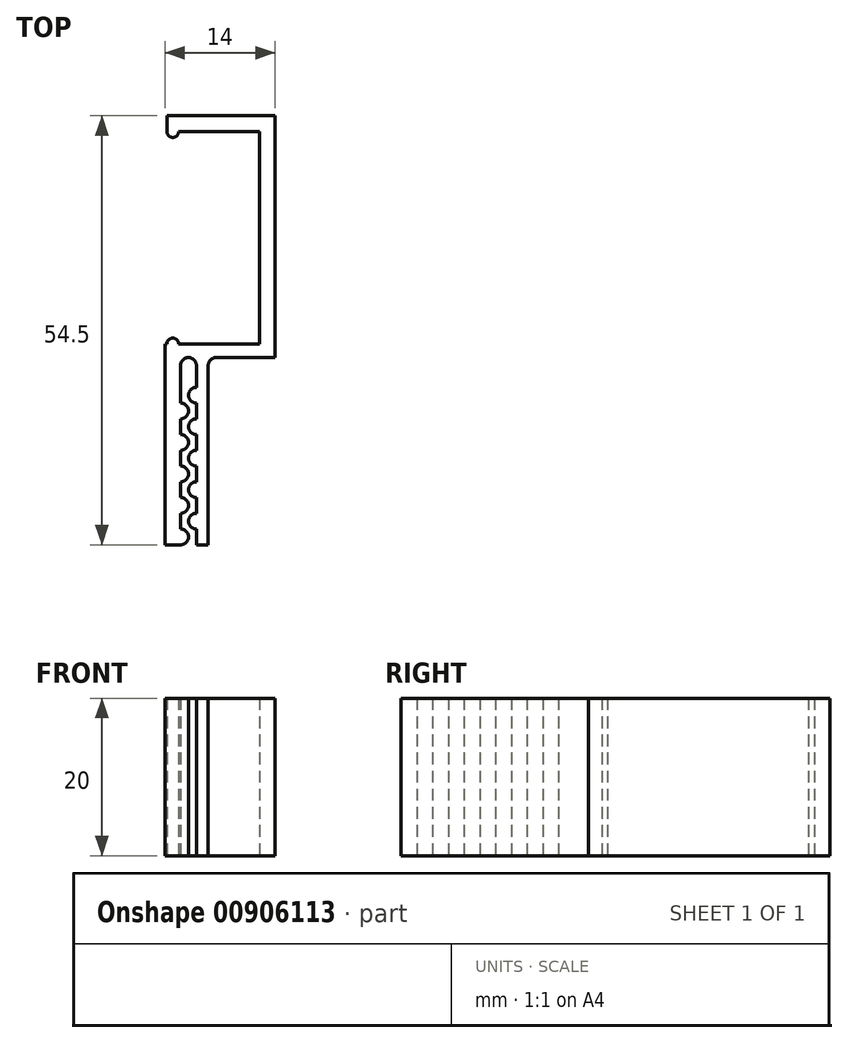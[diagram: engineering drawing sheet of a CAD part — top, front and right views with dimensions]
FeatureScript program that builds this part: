
annotation { "Feature Type Name" : "Feature", "Feature Type Description" : "" }
export const myFeature = defineFeature(function(context is Context, id is Id, definition is map)
    precondition{}
    {
        {
            var Q0;
            Q0=qCreatedBy(makeId("Top.planeOp"),FACE);
            var sketch = newSketch(context, id + "F0", { "sketchPlane" : qUnion([Q0])});
            skLineSegment(sketch, "E0", {"start": v(0, 0) * mm, "end": v(0, 25.5) * mm});
            skLineSegment(sketch, "E1", {"start": v(12, 25.5) * mm, "end": v(12, 52.5) * mm});
            skLineSegment(sketch, "E2", {"start": v(12, 52.5) * mm, "end": v(1.75, 52.5) * mm});
            skLineSegment(sketch, "E3.0", {"start": v(14, 54.5) * mm, "end": v(0.25, 54.5) * mm});
            skLineSegment(sketch, "E3.1", {"start": v(14, 23.78) * mm, "end": v(14, 54.5) * mm});
            skLineSegment(sketch, "E3.2", {"start": v(3, 23.78) * mm, "end": v(3, 23.78) * mm});
            skLineSegment(sketch, "E3.3", {"start": v(2, 2) * mm, "end": v(2, 5) * mm});
            skLineSegment(sketch, "E4", {"start": v(0, 0) * mm, "end": v(2, 0) * mm});
            skLineSegment(sketch, "E5.trimOffspring", {"start": v(1.75, 25.5) * mm, "end": v(12, 25.5) * mm});
            skLineSegment(sketch, "E6.0", {"start": v(4, 0) * mm, "end": v(4, 2) * mm});
            skLineSegment(sketch, "E7.0", {"start": v(5.5, 0) * mm, "end": v(5.5, 22.78) * mm});
            skLineSegment(sketch, "E8", {"start": v(4, 0) * mm, "end": v(5.5, 0) * mm});
            skLineSegment(sketch, "E9.trimOffspring", {"start": v(6.5, 23.78) * mm, "end": v(14, 23.78) * mm});
            skArc(sketch, "E10", {"start": v(2, 0) * mm, "mid": v(3, 1) * mm, "end": v(2, 2) * mm});
            skArc(sketch, "E11", {"start": v(4, 4) * mm, "mid": v(3, 3) * mm, "end": v(4, 2) * mm});
            skArc(sketch, "E12.0.1.0", {"start": v(2, 4) * mm, "mid": v(3, 5) * mm, "end": v(2, 6) * mm});
            skArc(sketch, "E12.0.1.1", {"start": v(4, 8) * mm, "mid": v(3, 7) * mm, "end": v(4, 6) * mm});
            skArc(sketch, "E12.0.2.0", {"start": v(2, 8) * mm, "mid": v(3, 9) * mm, "end": v(2, 10) * mm});
            skArc(sketch, "E12.0.2.1", {"start": v(4, 12) * mm, "mid": v(3, 11) * mm, "end": v(4, 10) * mm});
            skArc(sketch, "E12.0.3.0", {"start": v(2, 12) * mm, "mid": v(3, 13) * mm, "end": v(2, 14) * mm});
            skArc(sketch, "E12.0.3.1", {"start": v(4, 16) * mm, "mid": v(3, 15) * mm, "end": v(4, 14) * mm});
            skArc(sketch, "E12.0.4.0", {"start": v(2, 16) * mm, "mid": v(3, 17) * mm, "end": v(2, 18) * mm});
            skArc(sketch, "E12.0.4.1", {"start": v(4, 20) * mm, "mid": v(3, 19) * mm, "end": v(4, 18) * mm});
            skLineSegment(sketch, "E12.direction1", {"start": v(2, 1) * mm, "end": v(27, 1) * mm, "construction": true});
            skLineSegment(sketch, "E12.direction2", {"start": v(2, 2) * mm, "end": v(2, 4) * mm, "construction": true});
            skLineSegment(sketch, "E13.trimOffspring", {"start": v(4, 20) * mm, "end": v(4, 22.78) * mm});
            skLineSegment(sketch, "E14.trimOffspring", {"start": v(2, 18) * mm, "end": v(2, 22.78) * mm});
            skLineSegment(sketch, "E15.trimOffspring", {"start": v(4, 16) * mm, "end": v(4, 18) * mm});
            skLineSegment(sketch, "E16.trimOffspring", {"start": v(2, 14) * mm, "end": v(2, 16) * mm});
            skLineSegment(sketch, "E17.trimOffspring", {"start": v(4, 12) * mm, "end": v(4, 14) * mm});
            skLineSegment(sketch, "E18.trimOffspring", {"start": v(2, 10) * mm, "end": v(2, 12) * mm});
            skLineSegment(sketch, "E19.trimOffspring", {"start": v(4, 8) * mm, "end": v(4, 10) * mm});
            skLineSegment(sketch, "E20.trimOffspring", {"start": v(2, 6) * mm, "end": v(2, 8) * mm});
            skLineSegment(sketch, "E21.trimOffspring", {"start": v(4, 4) * mm, "end": v(4, 6) * mm});
            skPoint(sketch, "E22.visualSharp", {"position": v(4, 23.78) * mm});
            skArc(sketch, "E22.filletArc", {"start": v(4, 22.78) * mm, "mid": v(3.7, 23.48) * mm, "end": v(3, 23.78) * mm});
            skPoint(sketch, "E23.visualSharp", {"position": v(2, 23.78) * mm});
            skArc(sketch, "E23.filletArc", {"start": v(3, 23.78) * mm, "mid": v(2.3, 23.48) * mm, "end": v(2, 22.78) * mm});
            skPoint(sketch, "E24.visualSharp", {"position": v(5.5, 23.78) * mm});
            skArc(sketch, "E24.filletArc", {"start": v(6.5, 23.78) * mm, "mid": v(5.8, 23.48) * mm, "end": v(5.5, 22.78) * mm});
            skLineSegment(sketch, "E25", {"start": v(0.25, 54.5) * mm, "end": v(0.25, 52.5) * mm});
            skArc(sketch, "E26", {"start": v(1.75, 25.5) * mm, "mid": v(1, 26.25) * mm, "end": v(0.25, 25.5) * mm});
            skArc(sketch, "E27", {"start": v(0.25, 52.5) * mm, "mid": v(1, 51.75) * mm, "end": v(1.75, 52.5) * mm});
            skLineSegment(sketch, "E28", {"start": v(0.25, 25.5) * mm, "end": v(0, 25.5) * mm});
            skSolve(sketch);
        }
        {
            var Q0;
            Q0=makeQuery(id+"F0.imprint","IMPRINT",FACE,{"disambiguationData":[TD([[makeQuery(id+"F0.imprint","IMPRINT",EDGE,{"derivedFrom":sQuery(id+"F0.wireOp",EDGE,"E0")}),-1.0]])]});
            extrude(context, id + "F1", {"entities" : qUnion([Q0]), "depth" : 20 * mm, "offsetDistance" : 25 * mm});
        }
    });
